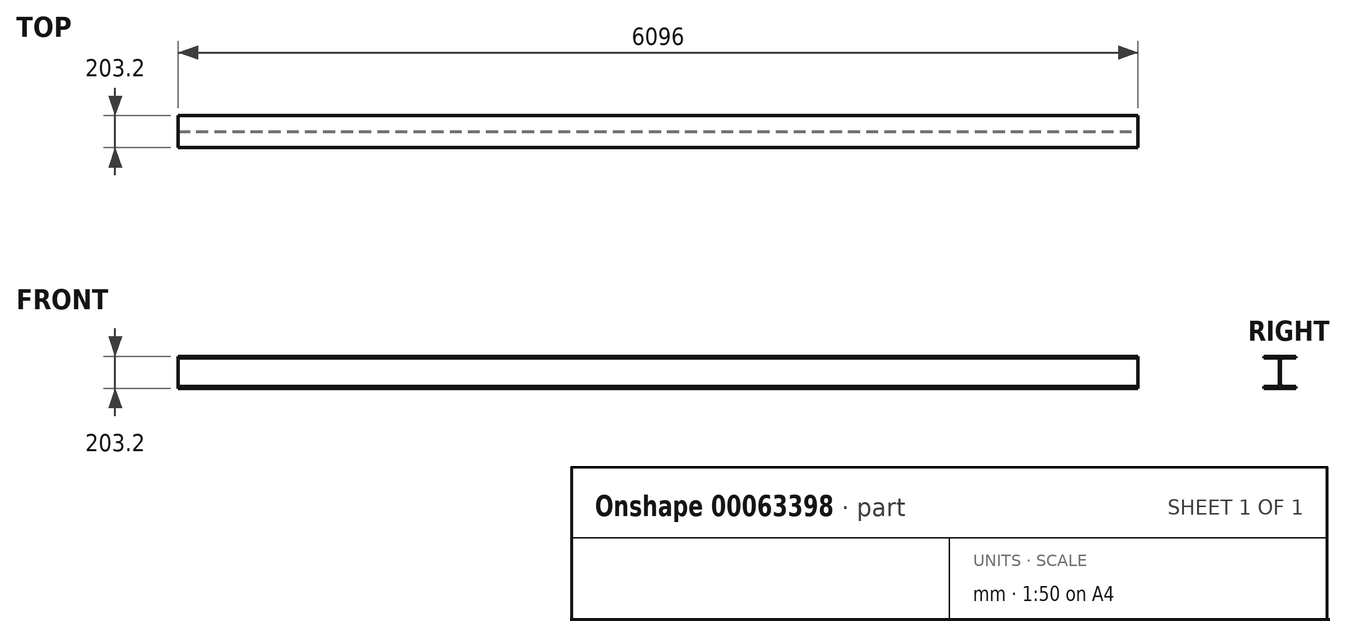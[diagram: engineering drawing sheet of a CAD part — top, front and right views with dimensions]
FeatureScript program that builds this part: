
annotation { "Feature Type Name" : "Feature", "Feature Type Description" : "" }
export const myFeature = defineFeature(function(context is Context, id is Id, definition is map)
    precondition{}
    {
        {
            var Q0;
            Q0=qCreatedBy(makeId("Right.planeOp"),FACE);
            var sketch = newSketch(context, id + "F0", { "sketchPlane" : qUnion([Q0])});
            skLineSegment(sketch, "E0", {"start": v(-3.6, 0) * mm, "end": v(-3.6, 73.6) * mm});
            skLineSegment(sketch, "E1", {"start": v(-20.6, 90.6) * mm, "end": v(-101.6, 90.6) * mm});
            skLineSegment(sketch, "E2", {"start": v(-101.6, 90.6) * mm, "end": v(-101.6, 101.6) * mm});
            skLineSegment(sketch, "E3", {"start": v(-101.6, 101.6) * mm, "end": v(0, 101.6) * mm});
            skPoint(sketch, "E4.visualSharp", {"position": v(-3.6, 90.6) * mm});
            skArc(sketch, "E4.filletArc", {"start": v(-3.6, 73.6) * mm, "mid": v(-8.58, 85.62) * mm, "end": v(-20.6, 90.6) * mm});
            skLineSegment(sketch, "E5.MirrorCS", {"start": v(3.6, 0) * mm, "end": v(3.6, 73.6) * mm});
            skLineSegment(sketch, "E6.MirrorCS", {"start": v(20.6, 90.6) * mm, "end": v(101.6, 90.6) * mm});
            skLineSegment(sketch, "E7.MirrorCS", {"start": v(101.6, 90.6) * mm, "end": v(101.6, 101.6) * mm});
            skArc(sketch, "E8.MirrorCS", {"start": v(3.6, 73.6) * mm, "mid": v(8.58, 85.62) * mm, "end": v(20.6, 90.6) * mm});
            skPoint(sketch, "E9.MirrorP", {"position": v(3.6, 90.6) * mm});
            skLineSegment(sketch, "E10.MirrorCS", {"start": v(101.6, 101.6) * mm, "end": v(0, 101.6) * mm});
            skPoint(sketch, "E11.MirrorP", {"position": v(3.6, -90.6) * mm});
            skLineSegment(sketch, "E12.MirrorCS", {"start": v(101.6, -101.6) * mm, "end": v(0, -101.6) * mm});
            skArc(sketch, "E13.MirrorCS", {"start": v(3.6, -73.6) * mm, "mid": v(8.58, -85.62) * mm, "end": v(20.6, -90.6) * mm});
            skLineSegment(sketch, "E14.MirrorCS", {"start": v(101.6, -90.6) * mm, "end": v(101.6, -101.6) * mm});
            skLineSegment(sketch, "E15.MirrorCS", {"start": v(20.6, -90.6) * mm, "end": v(101.6, -90.6) * mm});
            skLineSegment(sketch, "E16.MirrorCS", {"start": v(3.6, 0) * mm, "end": v(3.6, -73.6) * mm});
            skLineSegment(sketch, "E17.MirrorCS", {"start": v(-20.6, -90.6) * mm, "end": v(-101.6, -90.6) * mm});
            skArc(sketch, "E18.MirrorCS", {"start": v(-3.6, -73.6) * mm, "mid": v(-8.58, -85.62) * mm, "end": v(-20.6, -90.6) * mm});
            skLineSegment(sketch, "E19.MirrorCS", {"start": v(-3.6, 0) * mm, "end": v(-3.6, -73.6) * mm});
            skPoint(sketch, "E20.MirrorP", {"position": v(-3.6, -90.6) * mm});
            skLineSegment(sketch, "E21.MirrorCS", {"start": v(-101.6, -90.6) * mm, "end": v(-101.6, -101.6) * mm});
            skLineSegment(sketch, "E22.MirrorCS", {"start": v(-101.6, -101.6) * mm, "end": v(0, -101.6) * mm});
            skSolve(sketch);
        }
        {
            var Q0;
            Q0=makeQuery(id+"F0.imprint","IMPRINT",FACE,{"disambiguationData":[TD([[makeQuery(id+"F0.imprint","IMPRINT",EDGE,{"derivedFrom":sQuery(id+"F0.wireOp",EDGE,"E0")}),-1.0]])]});
            extrude(context, id + "F1", {"entities" : qUnion([Q0]), "oppositeDirection" : true, "depth" : 6096 * mm});
        }
    });
